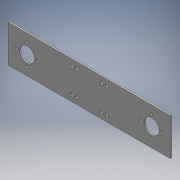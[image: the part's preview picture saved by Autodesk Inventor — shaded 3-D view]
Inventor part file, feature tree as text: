
AUTODESK INVENTOR PART (.ipt)
format: ipt  version: 2016 (Build 200138000, 138)  size: 149,504 bytes
history: native  units: mm
features: extrude x3, sketch x3, other x1
ambient origin geometry x8: Origin, YZ Plane, XZ Plane, XY Plane, X Axis, Y Axis, Z Axis, Center Point
bodies: Body1 (feature_tree)
feature tree (7):
  other  "ソリッド1"
  extrude  "押し出し1"  Depth=260.0mm
  extrude  "押し出し2"  Depth=60.0mm
  extrude  "押し出し3"  Depth=158.0mm
  sketch  "スケッチ1"
  sketch  "スケッチ2"
  sketch  "スケッチ3"
